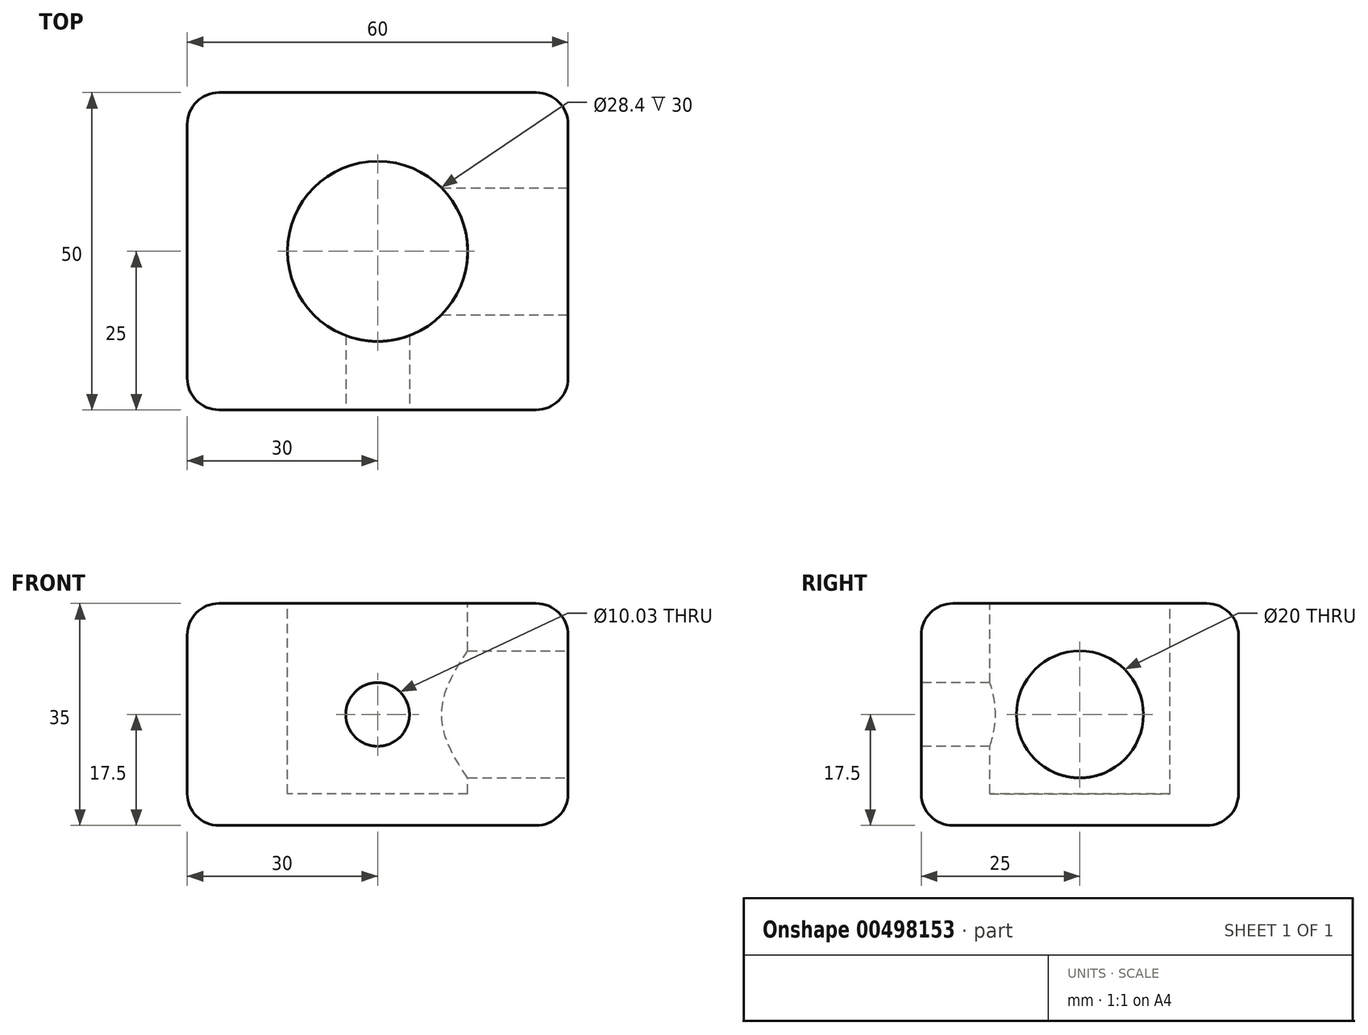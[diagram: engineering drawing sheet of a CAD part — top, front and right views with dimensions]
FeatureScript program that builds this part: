
annotation { "Feature Type Name" : "Feature", "Feature Type Description" : "" }
export const myFeature = defineFeature(function(context is Context, id is Id, definition is map)
    precondition{}
    {
        {
            var Q0;
            Q0=qCreatedBy(makeId("Top.planeOp"),FACE);
            var sketch = newSketch(context, id + "F0", { "sketchPlane" : qUnion([Q0])});
            skLineSegment(sketch, "E0.bottom", {"start": v(0, 0) * mm, "end": v(-60, 0) * mm});
            skLineSegment(sketch, "E0.top", {"start": v(0, 50) * mm, "end": v(-60, 50) * mm});
            skLineSegment(sketch, "E0.left", {"start": v(0, 0) * mm, "end": v(0, 50) * mm});
            skLineSegment(sketch, "E0.right", {"start": v(-60, 0) * mm, "end": v(-60, 50) * mm});
            skPoint(sketch, "E0.middle", {"position": v(-30, 25) * mm});
            skSolve(sketch);
        }
        {
            var Q0;
            Q0=makeQuery(id+"F0.imprint","IMPRINT",FACE,{"disambiguationData":[TD([[makeQuery(id+"F0.imprint","IMPRINT",EDGE,{"derivedFrom":sQuery(id+"F0.wireOp",EDGE,"E0.bottom")}),-1.0]])]});
            extrude(context, id + "F1", {"entities" : qUnion([Q0]), "depth" : 35 * mm});
        }
        {
            var Q0;
            Q0=makeQuery(id+"F1.opExtrude","CAP_EDGE",EDGE,{"disambiguationData":[OSD([sQuery(id+"F0.wireOp",EDGE,"E0.right")])],"isStart":false});
            var Q1;
            Q1=makeQuery(id+"F1.opExtrude","CAP_EDGE",EDGE,{"disambiguationData":[OSD([sQuery(id+"F0.wireOp",EDGE,"E0.top")])],"isStart":false});
            var Q2;
            Q2=makeQuery(id+"F1.opExtrude","CAP_EDGE",EDGE,{"disambiguationData":[OSD([sQuery(id+"F0.wireOp",EDGE,"E0.top")])],"isStart":true});
            var Q3;
            Q3=makeQuery(id+"F1.opExtrude","CAP_EDGE",EDGE,{"disambiguationData":[OSD([sQuery(id+"F0.wireOp",EDGE,"E0.right")])],"isStart":true});
            var Q4;
            Q4=makeQuery(id+"F1.opExtrude","SWEPT_EDGE",EDGE,{"disambiguationData":[OSD([sQuery(id+"F0.wireOp",EDGE,"E0.bottom"),sQuery(id+"F0.wireOp",EDGE,"E0.right")])]});
            var Q5;
            Q5=makeQuery(id+"F1.opExtrude","SWEPT_FACE",FACE,{"disambiguationData":[OSD([sQuery(id+"F0.wireOp",EDGE,"E0.top")])]});
            var Q6;
            Q6=makeQuery(id+"F1.opExtrude","SWEPT_EDGE",EDGE,{"disambiguationData":[OSD([sQuery(id+"F0.wireOp",EDGE,"E0.bottom"),sQuery(id+"F0.wireOp",EDGE,"E0.left")])]});
            var Q7;
            Q7=makeQuery(id+"F1.opExtrude","SWEPT_FACE",FACE,{"disambiguationData":[OSD([sQuery(id+"F0.wireOp",EDGE,"E0.left")])]});
            var Q8;
            Q8=makeQuery(id+"F1.opExtrude","CAP_EDGE",EDGE,{"disambiguationData":[OSD([sQuery(id+"F0.wireOp",EDGE,"E0.bottom")])],"isStart":false});
            var Q9;
            Q9=makeQuery(id+"F1.opExtrude","CAP_EDGE",EDGE,{"disambiguationData":[OSD([sQuery(id+"F0.wireOp",EDGE,"E0.bottom")])],"isStart":true});
            var Q10;
            Q10=makeQuery(id+"F1.opExtrude","SWEPT_FACE",FACE,{"disambiguationData":[OSD([sQuery(id+"F0.wireOp",EDGE,"E0.bottom")])]});
            fillet(context, id + "F2", {"entities" : qUnion([Q0, Q1, Q2, Q3, Q4, Q5, Q6, Q7, Q8, Q9, Q10]), "radius" : 5 * mm, "tangentPropagation" : true, "allowEdgeOverflow" : false});
        }
        {
            var Q0;
            Q0=makeQuery(id+"F1.opExtrude","SWEPT_FACE",FACE,{"disambiguationData":[OSD([sQuery(id+"F0.wireOp",EDGE,"E0.left")])]});
            var sketch = newSketch(context, id + "F3", { "sketchPlane" : qUnion([Q0])});
            skPoint(sketch, "E1.centerSnap0", {"position": v(45, 17.5) * mm});
            skPoint(sketch, "E1.centerSnap1", {"position": v(25, 30) * mm});
            skCircle(sketch, "E2", {"center": v(25, 17.5) * mm, "radius": 10 * mm});
            skSolve(sketch);
        }
        {
            var Q0;
            Q0=makeQuery(id+"F3.imprint","IMPRINT",FACE,{"disambiguationData":[TD([[makeQuery(id+"F3.imprint","IMPRINT",EDGE,{"derivedFrom":sQuery(id+"F3.wireOp",EDGE,"E2")}),1.0]])]});
            extrude(context, id + "F4", {"entities" : qUnion([Q0]), "operationType" : NewBodyOperationType.REMOVE, "oppositeDirection" : true, "depth" : 30 * mm});
        }
        {
            var Q0;
            Q0=makeQuery(id+"F1.opExtrude","CAP_FACE",FACE,{"disambiguationData":[OSD([sQuery(id+"F0.wireOp",EDGE,"E0.bottom"),sQuery(id+"F0.wireOp",EDGE,"E0.top"),sQuery(id+"F0.wireOp",EDGE,"E0.left"),sQuery(id+"F0.wireOp",EDGE,"E0.right")])],"isStart":false});
            var sketch = newSketch(context, id + "F5", { "sketchPlane" : qUnion([Q0])});
            skCircle(sketch, "E3", {"center": v(-30, 25) * mm, "radius": 14.2 * mm});
            skPoint(sketch, "E3.centerSnap0", {"position": v(-5, 25) * mm});
            skPoint(sketch, "E3.centerSnap1", {"position": v(-30, 45) * mm});
            skSolve(sketch);
        }
        {
            var Q0;
            Q0=makeQuery(id+"F5.imprint","IMPRINT",FACE,{"disambiguationData":[TD([[makeQuery(id+"F5.imprint","IMPRINT",EDGE,{"derivedFrom":sQuery(id+"F5.wireOp",EDGE,"E3")}),1.0]])]});
            extrude(context, id + "F6", {"entities" : qUnion([Q0]), "operationType" : NewBodyOperationType.REMOVE, "oppositeDirection" : true, "depth" : 30 * mm});
        }
        {
            var Q0;
            Q0=makeQuery(id+"F1.opExtrude","SWEPT_FACE",FACE,{"disambiguationData":[OSD([sQuery(id+"F0.wireOp",EDGE,"E0.bottom")])]});
            var sketch = newSketch(context, id + "F7", { "sketchPlane" : qUnion([Q0])});
            skCircle(sketch, "E4", {"center": v(-30, 17.5) * mm, "radius": 5.02 * mm});
            skPoint(sketch, "E4.centerSnap0", {"position": v(-55, 17.5) * mm});
            skPoint(sketch, "E4.centerSnap1", {"position": v(-30, 30) * mm});
            skSolve(sketch);
        }
        {
            var Q0;
            Q0=makeQuery(id+"F7.imprint","IMPRINT",FACE,{"disambiguationData":[TD([[makeQuery(id+"F7.imprint","IMPRINT",EDGE,{"derivedFrom":sQuery(id+"F7.wireOp",EDGE,"E4")}),1.0]])]});
            extrude(context, id + "F8", {"entities" : qUnion([Q0]), "operationType" : NewBodyOperationType.REMOVE, "oppositeDirection" : true, "depth" : 13.3 * mm});
        }
        {
            var Q0;
            Q0=makeQuery(id+"F1.opExtrude","SWEPT_FACE",FACE,{"disambiguationData":[OSD([sQuery(id+"F0.wireOp",EDGE,"E0.left")])]});
            var sketch = newSketch(context, id + "F9", { "sketchPlane" : qUnion([Q0])});
            skCircle(sketch, "E5", {"center": v(25, 17.5) * mm, "radius": 11.72 * mm});
            skSolve(sketch);
        }
        {
            var Q0;
            Q0=sQuery(id+"F9.wireOp",EDGE,"E5");
            extrude(context, id + "F10", {"bodyType" : ToolBodyType.SURFACE, "surfaceEntities" : qUnion([Q0]), "depth" : 64.5 * mm});
        }
    });
